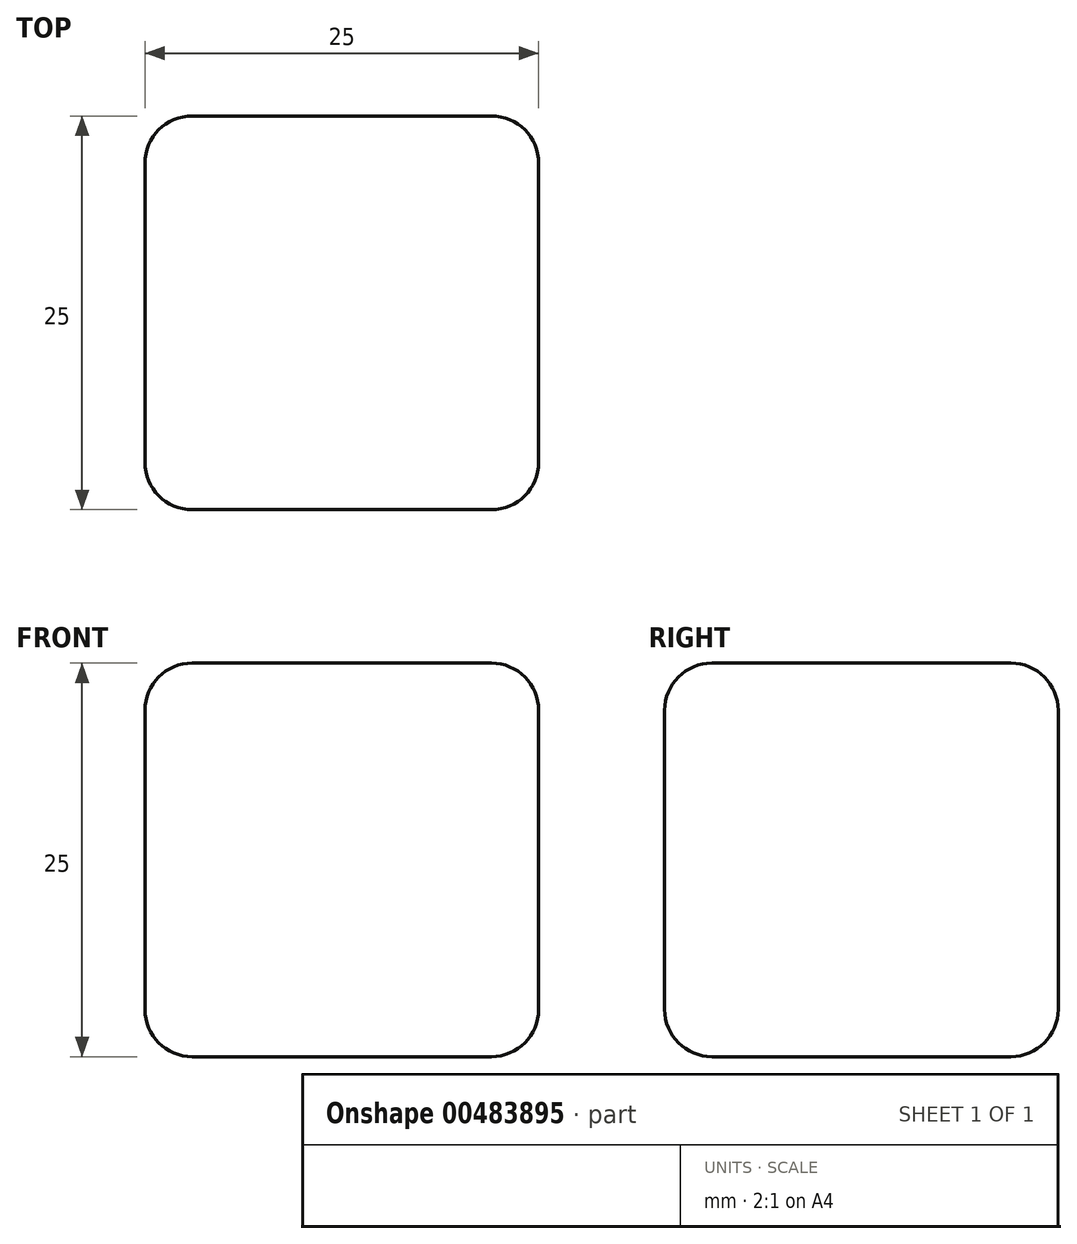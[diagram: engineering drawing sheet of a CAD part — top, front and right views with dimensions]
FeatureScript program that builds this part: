
annotation { "Feature Type Name" : "Feature", "Feature Type Description" : "" }
export const myFeature = defineFeature(function(context is Context, id is Id, definition is map)
    precondition{}
    {
        {
            var Q0;
            Q0=qCreatedBy(makeId("Top.planeOp"),FACE);
            var sketch = newSketch(context, id + "F0", { "sketchPlane" : qUnion([Q0])});
            skLineSegment(sketch, "E0.bottom", {"start": v(-12.5, 12.5) * mm, "end": v(12.5, 12.5) * mm});
            skLineSegment(sketch, "E0.top", {"start": v(-12.5, -12.5) * mm, "end": v(12.5, -12.5) * mm});
            skLineSegment(sketch, "E0.left", {"start": v(-12.5, 12.5) * mm, "end": v(-12.5, -12.5) * mm});
            skLineSegment(sketch, "E0.right", {"start": v(12.5, 12.5) * mm, "end": v(12.5, -12.5) * mm});
            skSolve(sketch);
        }
        {
            var Q0;
            Q0 = qSketchRegion(id + "FaGl0OoQbQYhOC2_0", true);
            var Q1;
            Q1 = qSketchRegion(id + "F0", true);
            extrude(context, id + "F1", {"entities" : qUnion([Q0, Q1]), "depth" : 25 * mm});
        }
        {
            var Q0;
            Q0=makeQuery(id+"F1.opExtrude","CAP_EDGE",EDGE,{"disambiguationData":[OSD([sQuery(id+"F0.wireOp",EDGE,"E0.right")])],"isStart":false});
            fillet(context, id + "F2", {"entities" : qUnion([Q0]), "radius" : 3 * mm, "tangentPropagation" : true, "allowEdgeOverflow" : false});
        }
        {
            var Q0;
            Q0=makeQuery(id+"F1.opExtrude","CAP_FACE",FACE,{"disambiguationData":[OSD([sQuery(id+"F0.wireOp",EDGE,"E0.bottom"),sQuery(id+"F0.wireOp",EDGE,"E0.top"),sQuery(id+"F0.wireOp",EDGE,"E0.left"),sQuery(id+"F0.wireOp",EDGE,"E0.right")])],"isStart":false});
            fillet(context, id + "F3", {"entities" : qUnion([Q0]), "radius" : 3 * mm, "tangentPropagation" : true, "allowEdgeOverflow" : false});
        }
        {
            var Q0;
            Q0=makeQuery(id+"F1.opExtrude","CAP_FACE",FACE,{"disambiguationData":[OSD([sQuery(id+"F0.wireOp",EDGE,"E0.bottom"),sQuery(id+"F0.wireOp",EDGE,"E0.top"),sQuery(id+"F0.wireOp",EDGE,"E0.left"),sQuery(id+"F0.wireOp",EDGE,"E0.right")])],"isStart":true});
            fillet(context, id + "F4", {"entities" : qUnion([Q0]), "radius" : 3 * mm, "tangentPropagation" : true, "allowEdgeOverflow" : false});
        }
        {
            var Q0;
            Q0=makeQuery(id+"F1.opExtrude","SWEPT_EDGE",EDGE,{"disambiguationData":[OSD([sQuery(id+"F0.wireOp",EDGE,"E0.bottom"),sQuery(id+"F0.wireOp",EDGE,"E0.left")])]});
            var Q1;
            Q1=makeQuery(id+"F1.opExtrude","SWEPT_EDGE",EDGE,{"disambiguationData":[OSD([sQuery(id+"F0.wireOp",EDGE,"E0.top"),sQuery(id+"F0.wireOp",EDGE,"E0.left")])]});
            fillet(context, id + "F5", {"entities" : qUnion([Q0, Q1]), "radius" : 3 * mm, "tangentPropagation" : true, "allowEdgeOverflow" : false});
        }
    });
